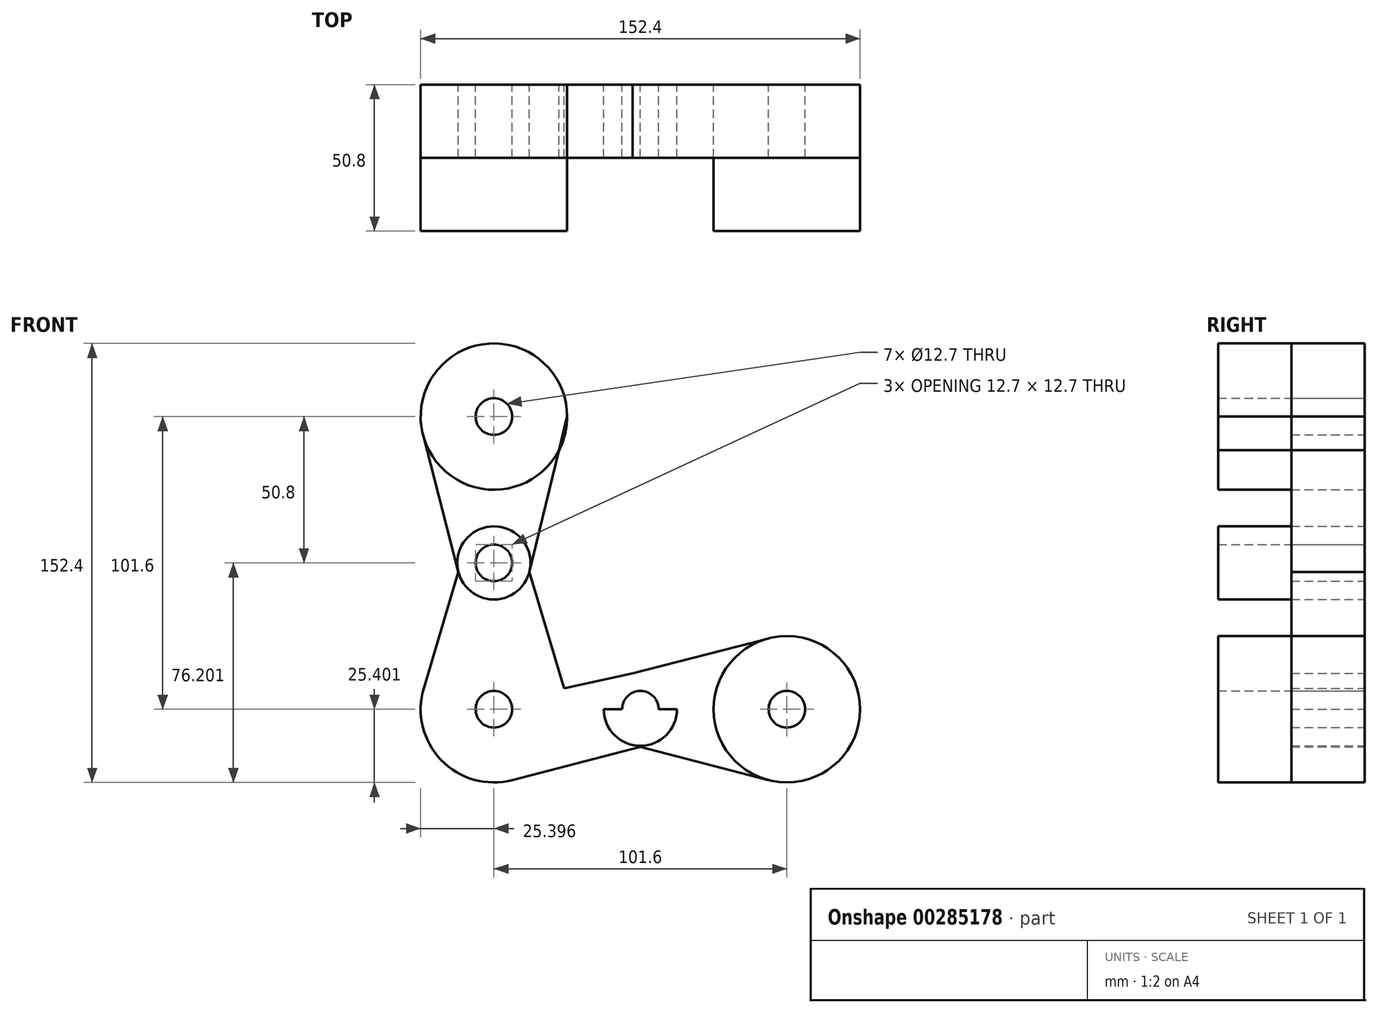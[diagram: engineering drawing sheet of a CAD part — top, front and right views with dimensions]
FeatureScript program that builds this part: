
annotation { "Feature Type Name" : "Feature", "Feature Type Description" : "" }
export const myFeature = defineFeature(function(context is Context, id is Id, definition is map)
    precondition{}
    {
        {
            var Q0;
            Q0=qCreatedBy(makeId("Front.planeOp"),FACE);
            var sketch = newSketch(context, id + "F0", { "sketchPlane" : qUnion([Q0])});
            skLineSegment(sketch, "E0", {"start": v(-76.69, -75.49) * mm, "end": v(-25.4, -75.49) * mm});
            skLineSegment(sketch, "E1", {"start": v(-76.2, -75.49) * mm, "end": v(-25.4, -75.49) * mm});
            skLineSegment(sketch, "E2", {"start": v(-76.2, -75.49) * mm, "end": v(-76.2, -24.69) * mm});
            skLineSegment(sketch, "E3", {"start": v(-76.2, -24.69) * mm, "end": v(-76.2, 26.11) * mm});
            skLineSegment(sketch, "E4", {"start": v(-25.4, -75.49) * mm, "end": v(25.4, -75.49) * mm});
            skCircle(sketch, "E5", {"center": v(-76.2, 26.11) * mm, "radius": 25.4 * mm});
            skCircle(sketch, "E6", {"center": v(-76.2, -75.49) * mm, "radius": 25.4 * mm});
            skCircle(sketch, "E7", {"center": v(25.4, -75.49) * mm, "radius": 25.4 * mm});
            skCircle(sketch, "E8", {"center": v(-76.2, -24.69) * mm, "radius": 12.7 * mm});
            skCircle(sketch, "E9", {"center": v(-25.4, -75.49) * mm, "radius": 12.7 * mm});
            skLineSegment(sketch, "E10", {"start": v(-100.79, 19.76) * mm, "end": v(-88.5, -27.86) * mm});
            skLineSegment(sketch, "E11", {"start": v(-88.5, -27.86) * mm, "end": v(-100.53, -68.23) * mm});
            skLineSegment(sketch, "E12", {"start": v(-50.8, 26.12) * mm, "end": v(-63.9, -27.86) * mm});
            skLineSegment(sketch, "E13", {"start": v(-63.9, -27.86) * mm, "end": v(-51.85, -68.23) * mm});
            skLineSegment(sketch, "E14", {"start": v(-51.85, -68.23) * mm, "end": v(-28.08, -63.08) * mm});
            skLineSegment(sketch, "E15", {"start": v(-28.08, -63.08) * mm, "end": v(19.05, -50.9) * mm});
            skLineSegment(sketch, "E16", {"start": v(-69.84, -100.08) * mm, "end": v(-25.4, -88.6) * mm});
            skLineSegment(sketch, "E17", {"start": v(-25.4, -88.6) * mm, "end": v(19.06, -100.08) * mm});
            skSolve(sketch);
        }
        {
            var Q0;
            {var subQ0=sQuery(id+"F0.wireOp",EDGE,"E5");var subQ1=makeQuery(id+"F0.imprint","INTERSECT",VERTEX,{"derivedFrom":[subQ0,sQuery(id+"F0.wireOp",EDGE,"E10")]});Q0=makeQuery(id+"F0.imprint","IMPRINT",FACE,{"disambiguationData":[TD([[makeQuery(id+"F0.imprint","IMPRINT",EDGE,{"disambiguationData":[TD([[subQ1,1.0]])],"derivedFrom":subQ0}),1.0]])]});}
            var Q1;
            {var subQ0=sQuery(id+"F0.wireOp",EDGE,"E3");var subQ1=sQuery(id+"F0.wireOp",EDGE,"E2");var subQ2=makeQuery(id+"F0.imprint","INTERSECT",VERTEX,{"derivedFrom":[subQ1,subQ0]});Q1=makeQuery(id+"F0.imprint","IMPRINT",FACE,{"disambiguationData":[TD([[makeQuery(id+"F0.imprint","IMPRINT",EDGE,{"disambiguationData":[TD([[subQ2,1.0]])],"derivedFrom":subQ1}),1.0]])]});}
            var Q2;
            {var subQ0=sQuery(id+"F0.wireOp",EDGE,"E3");var subQ1=sQuery(id+"F0.wireOp",EDGE,"E2");var subQ2=makeQuery(id+"F0.imprint","INTERSECT",VERTEX,{"derivedFrom":[subQ1,subQ0]});Q2=makeQuery(id+"F0.imprint","IMPRINT",FACE,{"disambiguationData":[TD([[makeQuery(id+"F0.imprint","IMPRINT",EDGE,{"disambiguationData":[TD([[subQ2,1.0]])],"derivedFrom":subQ1}),-1.0]])]});}
            var Q3;
            {var subQ3=sQuery(id+"F0.wireOp",EDGE,"E2");var subQ5=sQuery(id+"F0.wireOp",EDGE,"E1");var subQ6=makeQuery(id+"F0.imprint","INTERSECT",VERTEX,{"derivedFrom":[subQ5,subQ3]});Q3=makeQuery(id+"F0.imprint","IMPRINT",FACE,{"disambiguationData":[TD([[makeQuery(id+"F0.imprint","IMPRINT",EDGE,{"disambiguationData":[TD([[subQ6,-1.0]])],"derivedFrom":subQ5}),-1.0]])]});}
            var Q4;
            {var subQ0=sQuery(id+"F0.wireOp",EDGE,"E2");var subQ1=sQuery(id+"F0.wireOp",EDGE,"E1");var subQ2=makeQuery(id+"F0.imprint","INTERSECT",VERTEX,{"derivedFrom":[subQ1,subQ0]});Q4=makeQuery(id+"F0.imprint","IMPRINT",FACE,{"disambiguationData":[TD([[makeQuery(id+"F0.imprint","IMPRINT",EDGE,{"disambiguationData":[TD([[subQ2,-1.0]])],"derivedFrom":subQ1}),1.0]])]});}
            var Q5;
            {var subQ0=sQuery(id+"F0.wireOp",EDGE,"E4");var subQ1=sQuery(id+"F0.wireOp",EDGE,"E1");var subQ2=makeQuery(id+"F0.imprint","INTERSECT",VERTEX,{"derivedFrom":[subQ1,subQ0]});Q5=makeQuery(id+"F0.imprint","IMPRINT",FACE,{"disambiguationData":[TD([[makeQuery(id+"F0.imprint","IMPRINT",EDGE,{"disambiguationData":[TD([[subQ2,1.0]])],"derivedFrom":subQ1}),1.0]])]});}
            var Q6;
            {var subQ0=sQuery(id+"F0.wireOp",EDGE,"E4");var subQ1=sQuery(id+"F0.wireOp",EDGE,"E1");var subQ2=makeQuery(id+"F0.imprint","INTERSECT",VERTEX,{"derivedFrom":[subQ1,subQ0]});Q6=makeQuery(id+"F0.imprint","IMPRINT",FACE,{"disambiguationData":[TD([[makeQuery(id+"F0.imprint","IMPRINT",EDGE,{"disambiguationData":[TD([[subQ2,1.0]])],"derivedFrom":subQ1}),-1.0]])]});}
            var Q7;
            {var subQ0=sQuery(id+"F0.wireOp",EDGE,"E7");var subQ1=makeQuery(id+"F0.imprint","INTERSECT",VERTEX,{"derivedFrom":[subQ0,sQuery(id+"F0.wireOp",EDGE,"E15")]});Q7=makeQuery(id+"F0.imprint","IMPRINT",FACE,{"disambiguationData":[TD([[makeQuery(id+"F0.imprint","IMPRINT",EDGE,{"disambiguationData":[TD([[subQ1,-1.0]])],"derivedFrom":subQ0}),1.0]])]});}
            extrude(context, id + "F1", {"entities" : qUnion([Q0, Q1, Q2, Q3, Q4, Q5, Q6, Q7]), "depth" : 50.8 * mm});
        }
        {
            var Q0;
            Q0 = qSketchRegion(id + "F0", true);
            extrude(context, id + "F2", {"entities" : qUnion([Q0]), "depth" : 25.4 * mm});
        }
        {
            var Q0;
            Q0=sQuery(id+"F0.wireOp",VERTEX,"E3.end");
            var Q1;
            Q1=sQuery(id+"F0.wireOp",VERTEX,"E3.start");
            var Q2;
            Q2=sQuery(id+"F0.wireOp",VERTEX,"E6.center");
            var Q3;
            Q3=sQuery(id+"F0.wireOp",VERTEX,"E4.start");
            var Q4;
            Q4=sQuery(id+"F0.wireOp",VERTEX,"E4.end");
            var Q5;
            Q5=makeQuery(id+"F1.opExtrude","SWEPT_BODY",BODY,{"disambiguationData":[OSD([sQuery(id+"F0.wireOp",EDGE,"E5"),sQuery(id+"F0.wireOp",EDGE,"E12")])]});
            var Q6;
            Q6=makeQuery(id+"F2.opExtrude","SWEPT_BODY",BODY,{"disambiguationData":[OSD([sQuery(id+"F0.wireOp",EDGE,"E1"),sQuery(id+"F0.wireOp",EDGE,"E4"),sQuery(id+"F0.wireOp",EDGE,"E5"),sQuery(id+"F0.wireOp",EDGE,"E6"),sQuery(id+"F0.wireOp",EDGE,"E7"),sQuery(id+"F0.wireOp",EDGE,"E9"),sQuery(id+"F0.wireOp",EDGE,"E10"),sQuery(id+"F0.wireOp",EDGE,"E11"),sQuery(id+"F0.wireOp",EDGE,"E12"),sQuery(id+"F0.wireOp",EDGE,"E13"),sQuery(id+"F0.wireOp",EDGE,"E14"),sQuery(id+"F0.wireOp",EDGE,"E15"),sQuery(id+"F0.wireOp",EDGE,"E16"),sQuery(id+"F0.wireOp",EDGE,"E17")])]});
            var Q7;
            Q7=makeQuery(id+"F1.opExtrude","SWEPT_BODY",BODY,{"disambiguationData":[OSD([sQuery(id+"F0.wireOp",EDGE,"E8")])]});
            var Q8;
            Q8=makeQuery(id+"F1.opExtrude","SWEPT_BODY",BODY,{"disambiguationData":[OSD([sQuery(id+"F0.wireOp",EDGE,"E6")])]});
            var Q9;
            Q9=makeQuery(id+"F1.opExtrude","SWEPT_BODY",BODY,{"disambiguationData":[OSD([sQuery(id+"F0.wireOp",EDGE,"E9")])]});
            var Q10;
            Q10=makeQuery(id+"F1.opExtrude","SWEPT_BODY",BODY,{"disambiguationData":[OSD([sQuery(id+"F0.wireOp",EDGE,"E7")])]});
            hole(context, id + "F3", {"style" : HoleStyle.SIMPLE, "endStyle" : HoleEndStyle.THROUGH, "oppositeDirection" : true, "holeDiameter" : 12.7 * mm, "tappedDepth" : 12.7 * mm, "tapClearance" : 3, "locations" : qUnion([Q0, Q1, Q2, Q3, Q4]), "scope" : qUnion([Q5, Q6, Q7, Q8, Q9, Q10])});
        }
    });
